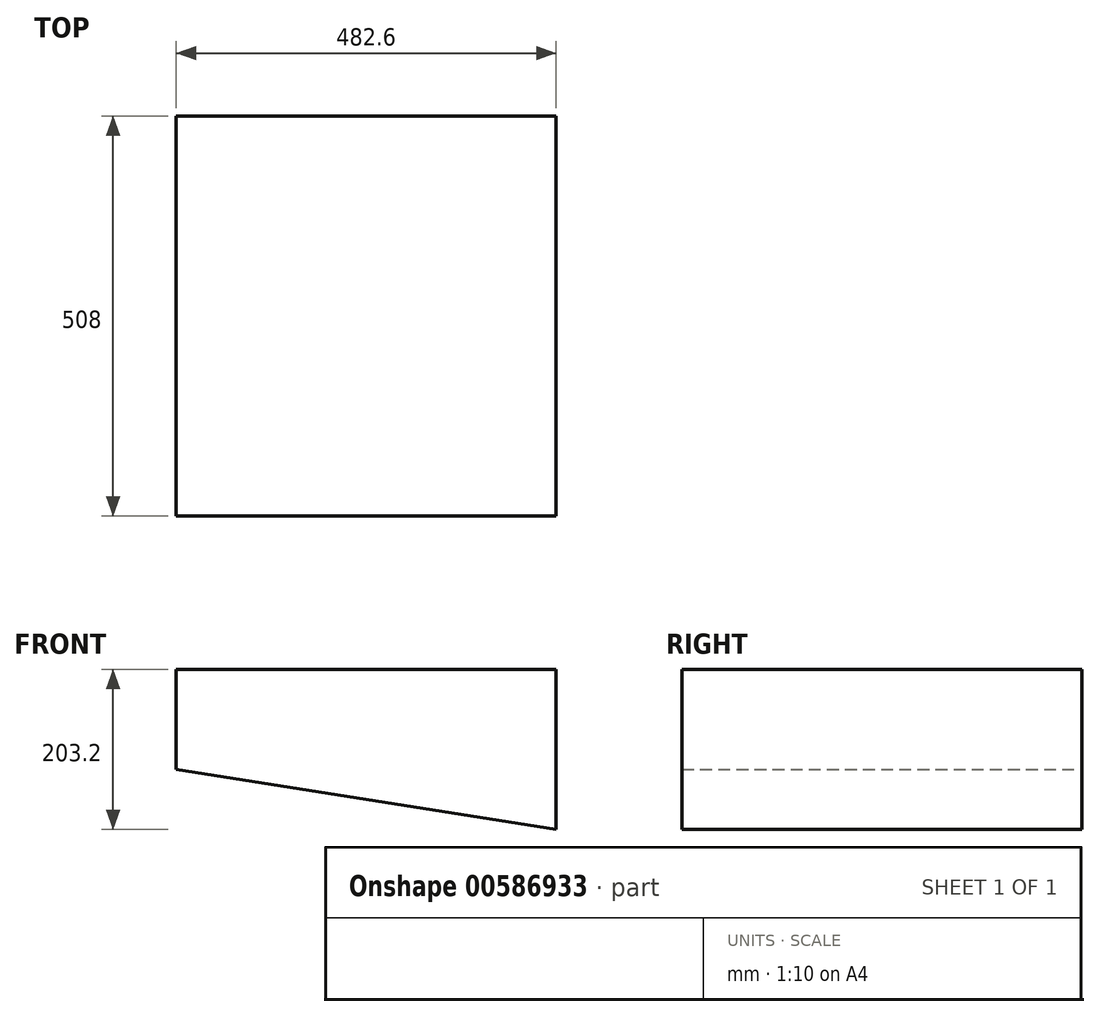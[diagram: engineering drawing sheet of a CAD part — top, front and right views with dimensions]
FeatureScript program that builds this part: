
annotation { "Feature Type Name" : "Feature", "Feature Type Description" : "" }
export const myFeature = defineFeature(function(context is Context, id is Id, definition is map)
    precondition{}
    {
        {
            var Q0;
            Q0=qCreatedBy(makeId("Front.planeOp"),FACE);
            var sketch = newSketch(context, id + "F0", { "sketchPlane" : qUnion([Q0])});
            skLineSegment(sketch, "E0", {"start": v(-207.62, 203.2) * mm, "end": v(274.98, 203.2) * mm});
            skLineSegment(sketch, "E1", {"start": v(274.98, 203.2) * mm, "end": v(274.98, 0) * mm});
            skLineSegment(sketch, "E2", {"start": v(274.98, 0) * mm, "end": v(-207.62, 76.2) * mm});
            skLineSegment(sketch, "E3", {"start": v(-207.62, 76.2) * mm, "end": v(-207.62, 203.2) * mm});
            skSolve(sketch);
        }
        {
            var Q0;
            Q0 = qSketchRegion(id + "F0", true);
            extrude(context, id + "F1", {"entities" : qUnion([Q0]), "depth" : 508 * mm, "offsetDistance" : 25.4 * mm});
        }
    });
